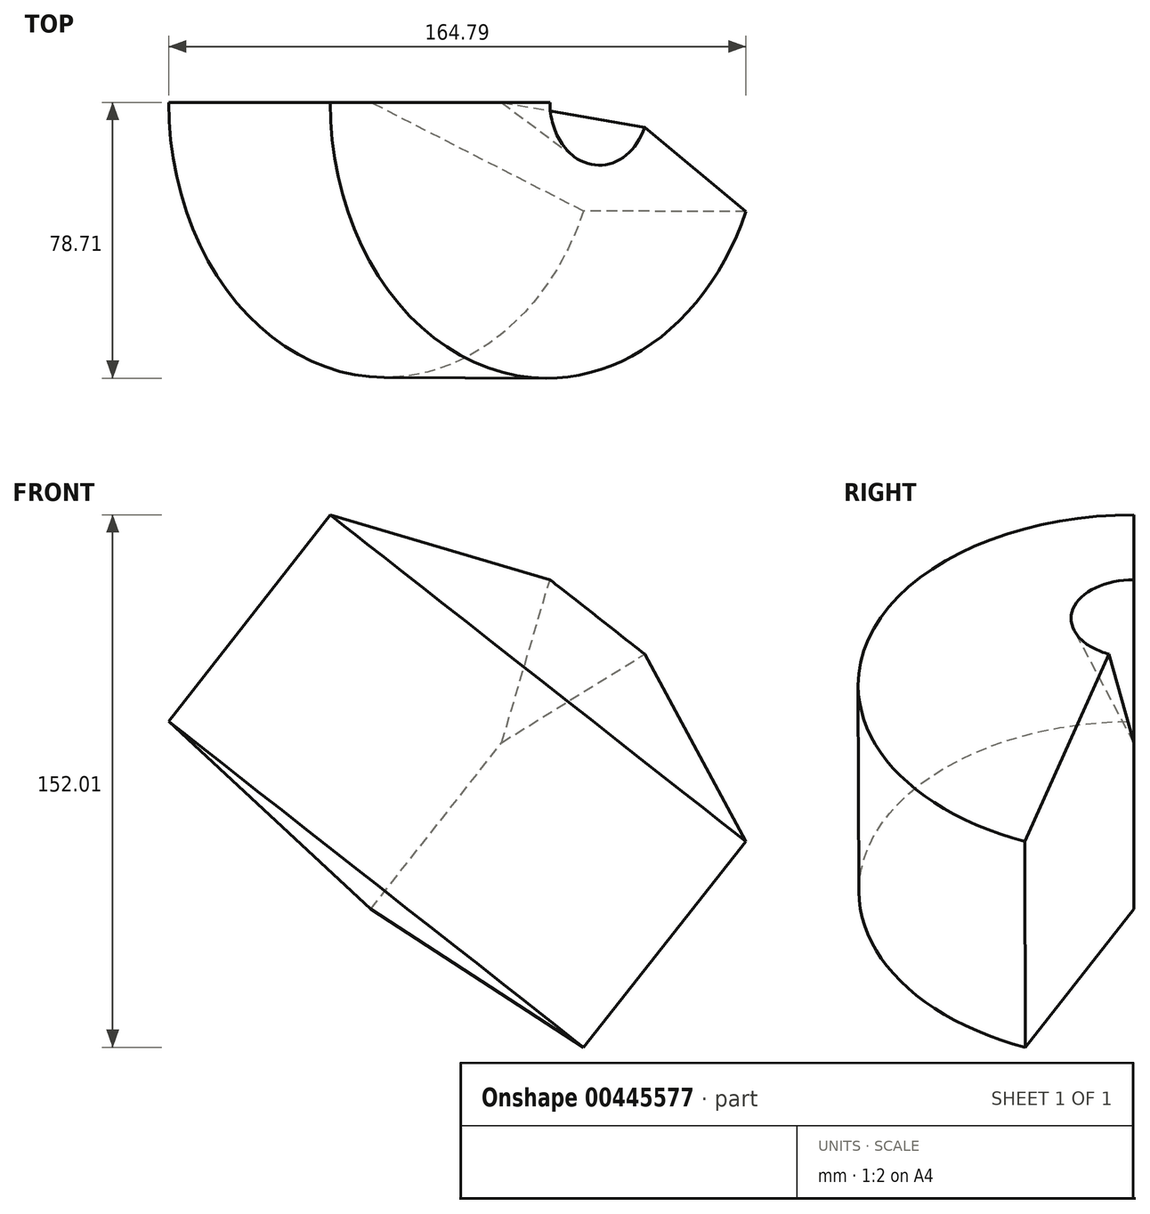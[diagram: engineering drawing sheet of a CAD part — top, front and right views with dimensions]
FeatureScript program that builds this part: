
annotation { "Feature Type Name" : "Feature", "Feature Type Description" : "" }
export const myFeature = defineFeature(function(context is Context, id is Id, definition is map)
    precondition{}
    {
        {
            var Q0;
            Q0=qCreatedBy(makeId("Front.planeOp"),FACE);
            var sketch = newSketch(context, id + "F0", { "sketchPlane" : qUnion([Q0])});
            skLineSegment(sketch, "E0", {"start": v(27.9, -15.8) * mm, "end": v(41.63, 30.7) * mm});
            skLineSegment(sketch, "E1", {"start": v(41.63, 30.7) * mm, "end": v(-21.1, 49.23) * mm});
            skLineSegment(sketch, "E2", {"start": v(-21.1, 49.23) * mm, "end": v(-67.17, -9.74) * mm});
            skLineSegment(sketch, "E3", {"start": v(-67.17, -9.74) * mm, "end": v(-9.45, -63.33) * mm});
            skLineSegment(sketch, "E4", {"start": v(-9.45, -63.33) * mm, "end": v(27.9, -15.8) * mm});
            skSolve(sketch);
        }
        {
            var Q0;
            Q0=makeQuery(id+"F0.imprint","IMPRINT",FACE,{"disambiguationData":[TD([[makeQuery(id+"F0.imprint","IMPRINT",EDGE,{"derivedFrom":sQuery(id+"F0.wireOp",EDGE,"E0")}),1.0]])]});
            var Q1;
            Q1=sQuery(id+"F0.wireOp",EDGE,"E4");
            revolve(context, id + "F1", {"entities" : qUnion([Q0]), "axis" : qUnion([Q1]), "revolveType" : RevolveType.ONE_DIRECTION, "angle" : 156.7 * degree});
        }
    });
